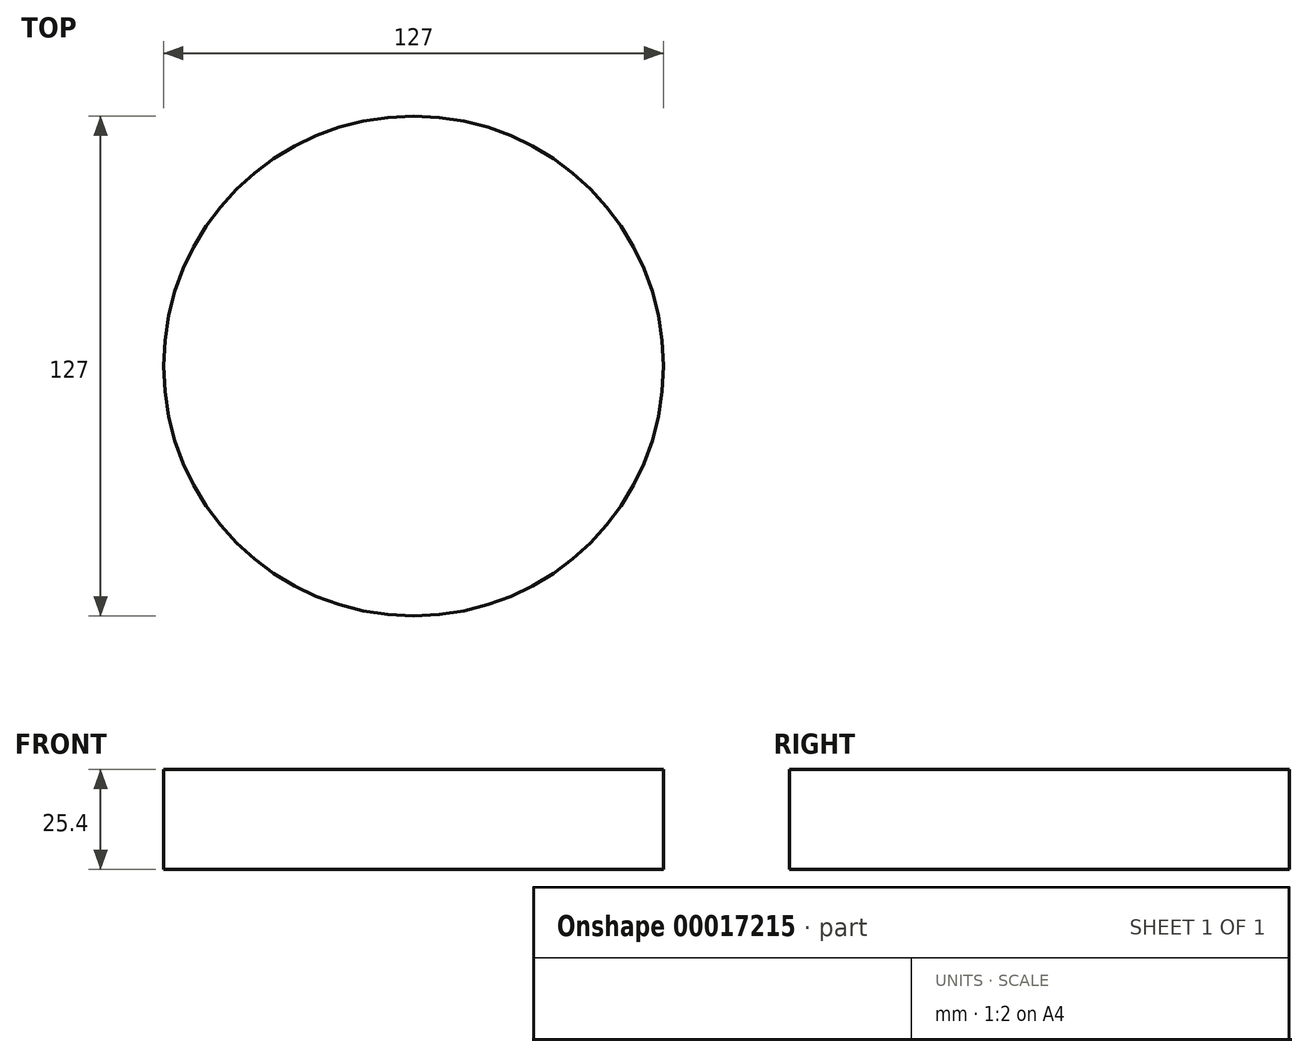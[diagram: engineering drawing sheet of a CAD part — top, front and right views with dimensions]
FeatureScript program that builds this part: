
annotation { "Feature Type Name" : "Feature", "Feature Type Description" : "" }
export const myFeature = defineFeature(function(context is Context, id is Id, definition is map)
    precondition{}
    {
        {
            var Q0;
            Q0=qCreatedBy(makeId("Top.planeOp"),FACE);
            var sketch = newSketch(context, id + "F0", { "sketchPlane" : qUnion([Q0])});
            skCircle(sketch, "E0", {"center": v(0, 0) * mm, "radius": 63.5 * mm});
            skSolve(sketch);
        }
        {
            var Q0;
            Q0=sQuery(id+"F0.wireOp",EDGE,"E0");
            extrude(context, id + "F1", {"bodyType" : ToolBodyType.SURFACE, "surfaceEntities" : qUnion([Q0]), "depth" : 25.4 * mm});
        }
    });
